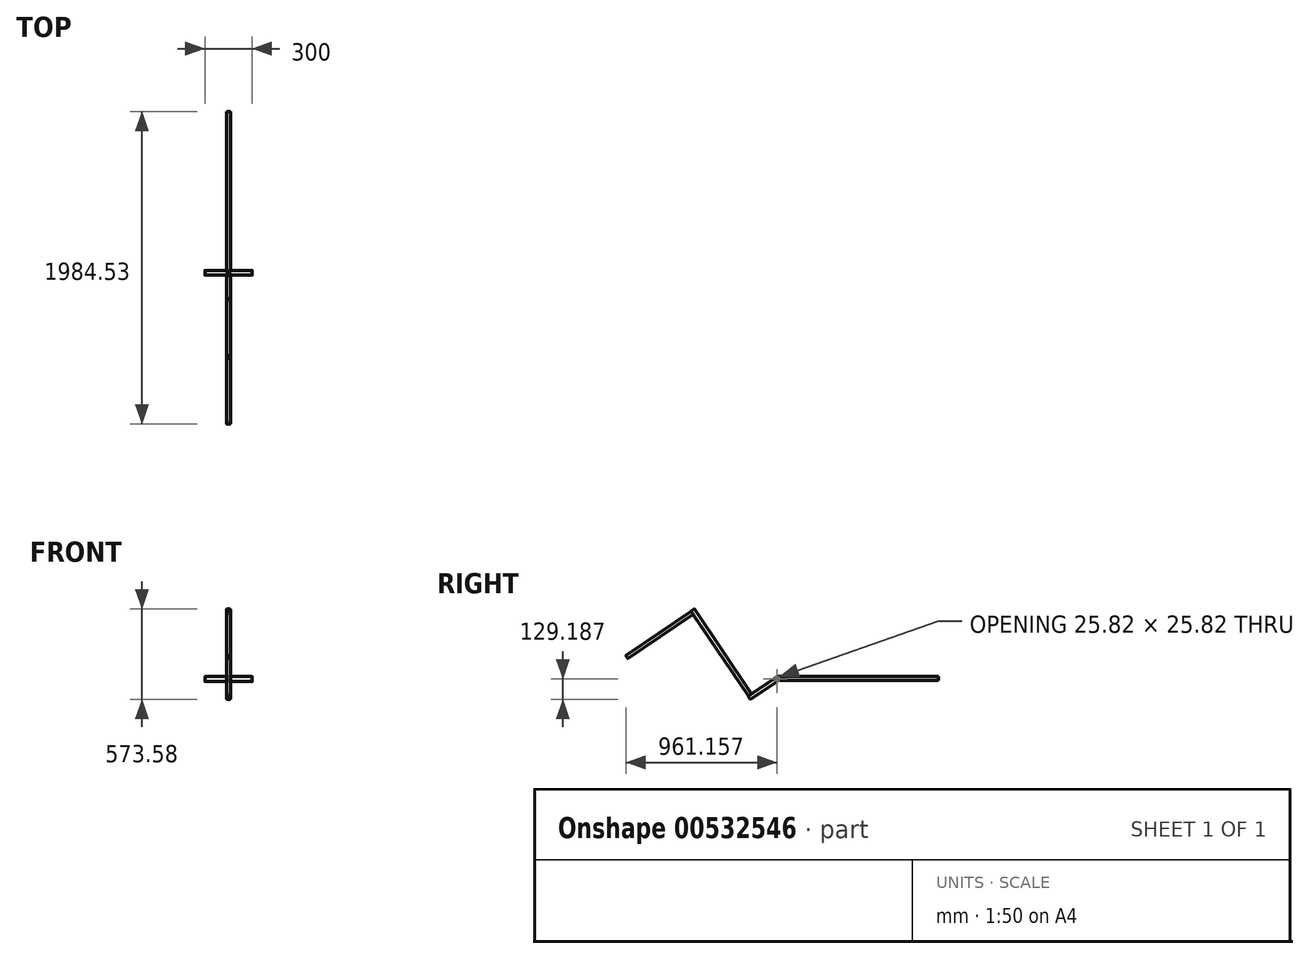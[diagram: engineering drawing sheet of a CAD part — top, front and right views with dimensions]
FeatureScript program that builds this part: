
annotation { "Feature Type Name" : "Feature", "Feature Type Description" : "" }
export const myFeature = defineFeature(function(context is Context, id is Id, definition is map)
    precondition{}
    {
        {
            var Q0;
            Q0=qCreatedBy(makeId("Front.planeOp"),FACE);
            var sketch = newSketch(context, id + "F0", { "sketchPlane" : qUnion([Q0])});
            skLineSegment(sketch, "E0.bottom", {"start": v(7.5, 12.5) * mm, "end": v(-7.5, 12.5) * mm});
            skLineSegment(sketch, "E0.top", {"start": v(7.5, -12.5) * mm, "end": v(-7.5, -12.5) * mm});
            skLineSegment(sketch, "E0.left", {"start": v(12.5, 7.5) * mm, "end": v(12.5, -7.5) * mm});
            skLineSegment(sketch, "E0.right", {"start": v(-12.5, 7.5) * mm, "end": v(-12.5, -7.5) * mm});
            skPoint(sketch, "E0.middle", {"position": v(0, 0) * mm});
            skPoint(sketch, "E1.visualSharp", {"position": v(-12.5, 12.5) * mm});
            skArc(sketch, "E1.filletArc", {"start": v(-7.5, 12.5) * mm, "mid": v(-11.04, 11.04) * mm, "end": v(-12.5, 7.5) * mm});
            skPoint(sketch, "E2.visualSharp", {"position": v(12.5, 12.5) * mm});
            skArc(sketch, "E2.filletArc", {"start": v(12.5, 7.5) * mm, "mid": v(11.04, 11.04) * mm, "end": v(7.5, 12.5) * mm});
            skPoint(sketch, "E3.visualSharp", {"position": v(12.5, -12.5) * mm});
            skArc(sketch, "E3.filletArc", {"start": v(7.5, -12.5) * mm, "mid": v(11.04, -11.04) * mm, "end": v(12.5, -7.5) * mm});
            skPoint(sketch, "E4.visualSharp", {"position": v(-12.5, -12.5) * mm});
            skArc(sketch, "E4.filletArc", {"start": v(-12.5, -7.5) * mm, "mid": v(-11.04, -11.04) * mm, "end": v(-7.5, -12.5) * mm});
            skArc(sketch, "E5.0", {"start": v(10, 7.5) * mm, "mid": v(9.27, 9.27) * mm, "end": v(7.5, 10) * mm});
            skLineSegment(sketch, "E5.1", {"start": v(10, 7.5) * mm, "end": v(10, -7.5) * mm});
            skLineSegment(sketch, "E5.2", {"start": v(7.5, 10) * mm, "end": v(-7.5, 10) * mm});
            skArc(sketch, "E5.3", {"start": v(7.5, -10) * mm, "mid": v(9.27, -9.27) * mm, "end": v(10, -7.5) * mm});
            skArc(sketch, "E5.4", {"start": v(-7.5, 10) * mm, "mid": v(-9.27, 9.27) * mm, "end": v(-10, 7.5) * mm});
            skLineSegment(sketch, "E5.5", {"start": v(-10, 7.5) * mm, "end": v(-10, -7.5) * mm});
            skArc(sketch, "E5.6", {"start": v(-10, -7.5) * mm, "mid": v(-9.27, -9.27) * mm, "end": v(-7.5, -10) * mm});
            skLineSegment(sketch, "E5.7", {"start": v(7.5, -10) * mm, "end": v(-7.5, -10) * mm});
            skSolve(sketch);
        }
        {
            var Q0;
            Q0 = qSketchRegion(id + "F0", true);
            extrude(context, id + "F1", {"entities" : qUnion([Q0]), "endBound" : BoundingType.SYMMETRIC, "depth" : 1020 * mm, "offsetDistance" : 25 * mm});
        }
        {
            var Q0;
            Q0=makeQuery(id+"F1.opExtrude","SWEPT_FACE",FACE,{"disambiguationData":[OSD([sQuery(id+"F0.wireOp",EDGE,"E0.left")])]});
            var sketch = newSketch(context, id + "F2", { "sketchPlane" : qUnion([Q0])});
            skLineSegment(sketch, "E6", {"start": v(-510, 12.5) * mm, "end": v(-493.14, -12.5) * mm});
            skLineSegment(sketch, "E7", {"start": v(-493.14, -12.5) * mm, "end": v(-510, -12.5) * mm});
            skLineSegment(sketch, "E8", {"start": v(-510, -12.5) * mm, "end": v(-510, 12.5) * mm});
            skSolve(sketch);
        }
        {
            var Q0;
            Q0 = qSketchRegion(id + "F2", true);
            extrude(context, id + "F3", {"entities" : qUnion([Q0]), "operationType" : NewBodyOperationType.REMOVE, "endBound" : BoundingType.THROUGH_ALL, "oppositeDirection" : true, "depth" : 25 * mm, "offsetDistance" : 25 * mm});
        }
        {
            var Q0;
            Q0=qCreatedBy(makeId("Right.planeOp"),FACE);
            var sketch = newSketch(context, id + "F4", { "sketchPlane" : qUnion([Q0])});
            skLineSegment(sketch, "E9.bottom", {"start": v(-500.17, -11.02) * mm, "end": v(-512.6, -19.4) * mm});
            skLineSegment(sketch, "E9.top", {"start": v(-514.15, 9.7) * mm, "end": v(-526.58, 1.32) * mm});
            skLineSegment(sketch, "E9.left", {"start": v(-498.82, -4.08) * mm, "end": v(-507.2, 8.35) * mm});
            skLineSegment(sketch, "E9.right", {"start": v(-519.54, -18.06) * mm, "end": v(-527.93, -5.63) * mm});
            skPoint(sketch, "E9.middle", {"position": v(-513.37, -4.85) * mm});
            skPoint(sketch, "E10.visualSharp", {"position": v(-530.73, -1.48) * mm});
            skArc(sketch, "E10.filletArc", {"start": v(-526.58, 1.32) * mm, "mid": v(-528.7, -1.88) * mm, "end": v(-527.93, -5.63) * mm});
            skPoint(sketch, "E11.visualSharp", {"position": v(-510, 12.5) * mm});
            skArc(sketch, "E11.filletArc", {"start": v(-507.2, 8.35) * mm, "mid": v(-510.4, 10.47) * mm, "end": v(-514.15, 9.7) * mm});
            skPoint(sketch, "E12.visualSharp", {"position": v(-496.02, -8.23) * mm});
            skArc(sketch, "E12.filletArc", {"start": v(-500.17, -11.02) * mm, "mid": v(-498.05, -7.83) * mm, "end": v(-498.82, -4.08) * mm});
            skPoint(sketch, "E13.visualSharp", {"position": v(-516.75, -22.2) * mm});
            skArc(sketch, "E13.filletArc", {"start": v(-519.54, -18.06) * mm, "mid": v(-516.35, -20.17) * mm, "end": v(-512.6, -19.4) * mm});
            skArc(sketch, "E14.0", {"start": v(-509.28, 6.96) * mm, "mid": v(-510.87, 8.01) * mm, "end": v(-512.75, 7.63) * mm});
            skLineSegment(sketch, "E14.1", {"start": v(-500.89, -5.48) * mm, "end": v(-509.28, 6.96) * mm});
            skLineSegment(sketch, "E14.2", {"start": v(-512.75, 7.63) * mm, "end": v(-525.18, -0.76) * mm});
            skArc(sketch, "E14.3", {"start": v(-501.56, -8.95) * mm, "mid": v(-500.5, -7.35) * mm, "end": v(-500.89, -5.48) * mm});
            skArc(sketch, "E14.4", {"start": v(-525.18, -0.76) * mm, "mid": v(-526.24, -2.35) * mm, "end": v(-525.86, -4.23) * mm});
            skLineSegment(sketch, "E14.5", {"start": v(-517.47, -16.66) * mm, "end": v(-525.86, -4.23) * mm});
            skArc(sketch, "E14.6", {"start": v(-517.47, -16.66) * mm, "mid": v(-515.87, -17.72) * mm, "end": v(-514, -17.34) * mm});
            skLineSegment(sketch, "E14.7", {"start": v(-501.56, -8.95) * mm, "end": v(-514, -17.34) * mm});
            skSolve(sketch);
        }
        {
            var Q0;
            Q0 = qSketchRegion(id + "F4", true);
            extrude(context, id + "F5", {"entities" : qUnion([Q0]), "endBound" : BoundingType.SYMMETRIC, "depth" : 300 * mm, "offsetDistance" : 25 * mm});
        }
        {
            var Q0;
            Q0=makeQuery(id+"F5.opExtrude","SWEPT_FACE",FACE,{"disambiguationData":[OSD([sQuery(id+"F4.wireOp",EDGE,"E9.right")])]});
            var sketch = newSketch(context, id + "F6", { "sketchPlane" : qUnion([Q0])});
            skLineSegment(sketch, "E15", {"start": v(-150, 283.05) * mm, "end": v(150, 283.05) * mm, "construction": true});
            skLineSegment(sketch, "E16.bottom", {"start": v(7.5, 295.55) * mm, "end": v(-7.5, 295.55) * mm});
            skLineSegment(sketch, "E16.top", {"start": v(7.5, 270.55) * mm, "end": v(-7.5, 270.55) * mm});
            skLineSegment(sketch, "E16.left", {"start": v(12.5, 290.55) * mm, "end": v(12.5, 275.55) * mm});
            skLineSegment(sketch, "E16.right", {"start": v(-12.5, 290.55) * mm, "end": v(-12.5, 275.55) * mm});
            skPoint(sketch, "E16.middle", {"position": v(0, 283.05) * mm});
            skPoint(sketch, "E17.visualSharp", {"position": v(-12.5, 295.55) * mm});
            skArc(sketch, "E17.filletArc", {"start": v(-7.5, 295.55) * mm, "mid": v(-11.04, 294.09) * mm, "end": v(-12.5, 290.55) * mm});
            skPoint(sketch, "E18.visualSharp", {"position": v(12.5, 295.55) * mm});
            skArc(sketch, "E18.filletArc", {"start": v(12.5, 290.55) * mm, "mid": v(11.04, 294.09) * mm, "end": v(7.5, 295.55) * mm});
            skPoint(sketch, "E19.visualSharp", {"position": v(12.5, 270.55) * mm});
            skArc(sketch, "E19.filletArc", {"start": v(7.5, 270.55) * mm, "mid": v(11.04, 272.02) * mm, "end": v(12.5, 275.55) * mm});
            skPoint(sketch, "E20.visualSharp", {"position": v(-12.5, 270.55) * mm});
            skArc(sketch, "E20.filletArc", {"start": v(-12.5, 275.55) * mm, "mid": v(-11.04, 272.02) * mm, "end": v(-7.5, 270.55) * mm});
            skLineSegment(sketch, "E21.0", {"start": v(7.5, 293.05) * mm, "end": v(-7.5, 293.05) * mm});
            skArc(sketch, "E21.1", {"start": v(10, 290.55) * mm, "mid": v(9.27, 292.32) * mm, "end": v(7.5, 293.05) * mm});
            skArc(sketch, "E21.2", {"start": v(-7.5, 293.05) * mm, "mid": v(-9.27, 292.32) * mm, "end": v(-10, 290.55) * mm});
            skLineSegment(sketch, "E21.3", {"start": v(10, 290.55) * mm, "end": v(10, 275.55) * mm});
            skLineSegment(sketch, "E21.4", {"start": v(-10, 290.55) * mm, "end": v(-10, 275.55) * mm});
            skArc(sketch, "E21.5", {"start": v(-10, 275.55) * mm, "mid": v(-9.27, 273.78) * mm, "end": v(-7.5, 273.05) * mm});
            skLineSegment(sketch, "E21.6", {"start": v(7.5, 273.05) * mm, "end": v(-7.5, 273.05) * mm});
            skArc(sketch, "E21.7", {"start": v(7.5, 273.05) * mm, "mid": v(9.27, 273.78) * mm, "end": v(10, 275.55) * mm});
            skSolve(sketch);
        }
        {
            var Q0;
            Q0 = qSketchRegion(id + "F6", true);
            extrude(context, id + "F7", {"entities" : qUnion([Q0]), "depth" : 200 * mm, "offsetDistance" : 25 * mm});
        }
        {
            var Q0;
            Q0=makeQuery(id+"F7.opExtrude","SWEPT_FACE",FACE,{"disambiguationData":[OSD([sQuery(id+"F6.wireOp",EDGE,"E16.bottom")])]});
            var sketch = newSketch(context, id + "F8", { "sketchPlane" : qUnion([Q0])});
            skLineSegment(sketch, "E22", {"start": v(0, -640.82) * mm, "end": v(0, -628.32) * mm, "construction": true});
            skPoint(sketch, "E22.endSnap0", {"position": v(0, -640.82) * mm});
            skLineSegment(sketch, "E23.bottom", {"start": v(7.5, -640.82) * mm, "end": v(-7.5, -640.82) * mm});
            skLineSegment(sketch, "E23.top", {"start": v(7.5, -615.82) * mm, "end": v(-7.5, -615.82) * mm});
            skLineSegment(sketch, "E23.left", {"start": v(12.5, -635.82) * mm, "end": v(12.5, -620.82) * mm});
            skLineSegment(sketch, "E23.right", {"start": v(-12.5, -635.82) * mm, "end": v(-12.5, -620.82) * mm});
            skPoint(sketch, "E23.middle", {"position": v(0, -628.32) * mm});
            skPoint(sketch, "E24.visualSharp", {"position": v(-12.5, -615.82) * mm});
            skArc(sketch, "E24.filletArc", {"start": v(-7.5, -615.82) * mm, "mid": v(-11.04, -617.28) * mm, "end": v(-12.5, -620.82) * mm});
            skPoint(sketch, "E25.visualSharp", {"position": v(12.5, -615.82) * mm});
            skArc(sketch, "E25.filletArc", {"start": v(12.5, -620.82) * mm, "mid": v(11.04, -617.28) * mm, "end": v(7.5, -615.82) * mm});
            skPoint(sketch, "E26.visualSharp", {"position": v(12.5, -640.82) * mm});
            skArc(sketch, "E26.filletArc", {"start": v(7.5, -640.82) * mm, "mid": v(11.04, -639.35) * mm, "end": v(12.5, -635.82) * mm});
            skPoint(sketch, "E27.visualSharp", {"position": v(-12.5, -640.82) * mm});
            skArc(sketch, "E27.filletArc", {"start": v(-12.5, -635.82) * mm, "mid": v(-11.04, -639.35) * mm, "end": v(-7.5, -640.82) * mm});
            skArc(sketch, "E28.0", {"start": v(10, -620.82) * mm, "mid": v(9.27, -619.05) * mm, "end": v(7.5, -618.32) * mm});
            skLineSegment(sketch, "E28.1", {"start": v(10, -635.82) * mm, "end": v(10, -620.82) * mm});
            skLineSegment(sketch, "E28.2", {"start": v(7.5, -618.32) * mm, "end": v(-7.5, -618.32) * mm});
            skArc(sketch, "E28.3", {"start": v(7.5, -638.32) * mm, "mid": v(9.27, -637.59) * mm, "end": v(10, -635.82) * mm});
            skArc(sketch, "E28.4", {"start": v(-7.5, -618.32) * mm, "mid": v(-9.27, -619.05) * mm, "end": v(-10, -620.82) * mm});
            skLineSegment(sketch, "E28.5", {"start": v(-10, -635.82) * mm, "end": v(-10, -620.82) * mm});
            skArc(sketch, "E28.6", {"start": v(-10, -635.82) * mm, "mid": v(-9.27, -637.59) * mm, "end": v(-7.5, -638.32) * mm});
            skLineSegment(sketch, "E28.7", {"start": v(7.5, -638.32) * mm, "end": v(-7.5, -638.32) * mm});
            skSolve(sketch);
        }
        {
            var Q0;
            Q0 = qSketchRegion(id + "F8", true);
            extrude(context, id + "F9", {"entities" : qUnion([Q0]), "operationType" : NewBodyOperationType.ADD, "depth" : 650 * mm, "offsetDistance" : 25 * mm});
        }
        {
            var Q0;
            Q0=makeQuery(id+"F9.boolean.opBoolean","MERGE",FACE,{"derivedFrom":[makeQuery(id+"F7.opExtrude","CAP_FACE",FACE,{"disambiguationData":[OSD([sQuery(id+"F6.wireOp",EDGE,"E16.bottom"),sQuery(id+"F6.wireOp",EDGE,"E16.top"),sQuery(id+"F6.wireOp",EDGE,"E16.left"),sQuery(id+"F6.wireOp",EDGE,"E16.right"),sQuery(id+"F6.wireOp",EDGE,"E17.filletArc"),sQuery(id+"F6.wireOp",EDGE,"E18.filletArc"),sQuery(id+"F6.wireOp",EDGE,"E19.filletArc"),sQuery(id+"F6.wireOp",EDGE,"E20.filletArc"),sQuery(id+"F6.wireOp",EDGE,"E21.0"),sQuery(id+"F6.wireOp",EDGE,"E21.1"),sQuery(id+"F6.wireOp",EDGE,"E21.2"),sQuery(id+"F6.wireOp",EDGE,"E21.3"),sQuery(id+"F6.wireOp",EDGE,"E21.4"),sQuery(id+"F6.wireOp",EDGE,"E21.5"),sQuery(id+"F6.wireOp",EDGE,"E21.6"),sQuery(id+"F6.wireOp",EDGE,"E21.7")])],"isStart":false}),makeQuery(id+"F9.opExtrude","SWEPT_FACE",FACE,{"disambiguationData":[OSD([sQuery(id+"F8.wireOp",EDGE,"E23.bottom")])]})]});
            var sketch = newSketch(context, id + "F10", { "sketchPlane" : qUnion([Q0])});
            skLineSegment(sketch, "E29.bottom", {"start": v(7.5, 945.55) * mm, "end": v(-7.5, 945.55) * mm});
            skLineSegment(sketch, "E29.top", {"start": v(7.5, 920.55) * mm, "end": v(-7.5, 920.55) * mm});
            skLineSegment(sketch, "E29.left", {"start": v(12.5, 940.55) * mm, "end": v(12.5, 925.55) * mm});
            skLineSegment(sketch, "E29.right", {"start": v(-12.5, 940.55) * mm, "end": v(-12.5, 925.55) * mm});
            skPoint(sketch, "E29.middle", {"position": v(0, 933.05) * mm});
            skPoint(sketch, "E30.visualSharp", {"position": v(-12.5, 945.55) * mm});
            skArc(sketch, "E30.filletArc", {"start": v(-7.5, 945.55) * mm, "mid": v(-11.04, 944.09) * mm, "end": v(-12.5, 940.55) * mm});
            skPoint(sketch, "E31.visualSharp", {"position": v(12.5, 945.55) * mm});
            skArc(sketch, "E31.filletArc", {"start": v(12.5, 940.55) * mm, "mid": v(11.04, 944.09) * mm, "end": v(7.5, 945.55) * mm});
            skPoint(sketch, "E32.visualSharp", {"position": v(12.5, 920.55) * mm});
            skArc(sketch, "E32.filletArc", {"start": v(7.5, 920.55) * mm, "mid": v(11.04, 922.02) * mm, "end": v(12.5, 925.55) * mm});
            skPoint(sketch, "E33.visualSharp", {"position": v(-12.5, 920.55) * mm});
            skArc(sketch, "E33.filletArc", {"start": v(-12.5, 925.55) * mm, "mid": v(-11.04, 922.02) * mm, "end": v(-7.5, 920.55) * mm});
            skLineSegment(sketch, "E34.0", {"start": v(10, 940.55) * mm, "end": v(10, 925.55) * mm});
            skArc(sketch, "E34.1", {"start": v(7.5, 923.05) * mm, "mid": v(9.27, 923.78) * mm, "end": v(10, 925.55) * mm});
            skArc(sketch, "E34.2", {"start": v(10, 940.55) * mm, "mid": v(9.27, 942.32) * mm, "end": v(7.5, 943.05) * mm});
            skLineSegment(sketch, "E34.3", {"start": v(7.5, 923.05) * mm, "end": v(-7.5, 923.05) * mm});
            skLineSegment(sketch, "E34.4", {"start": v(7.5, 943.05) * mm, "end": v(-7.5, 943.05) * mm});
            skArc(sketch, "E34.5", {"start": v(-7.5, 943.05) * mm, "mid": v(-9.27, 942.32) * mm, "end": v(-10, 940.55) * mm});
            skLineSegment(sketch, "E34.6", {"start": v(-10, 940.55) * mm, "end": v(-10, 925.55) * mm});
            skArc(sketch, "E34.7", {"start": v(-10, 925.55) * mm, "mid": v(-9.27, 923.78) * mm, "end": v(-7.5, 923.05) * mm});
            skSolve(sketch);
        }
        {
            var Q0;
            Q0 = qSketchRegion(id + "F10", true);
            extrude(context, id + "F11", {"entities" : qUnion([Q0]), "operationType" : NewBodyOperationType.ADD, "depth" : 500 * mm, "offsetDistance" : 25 * mm});
        }
    });
